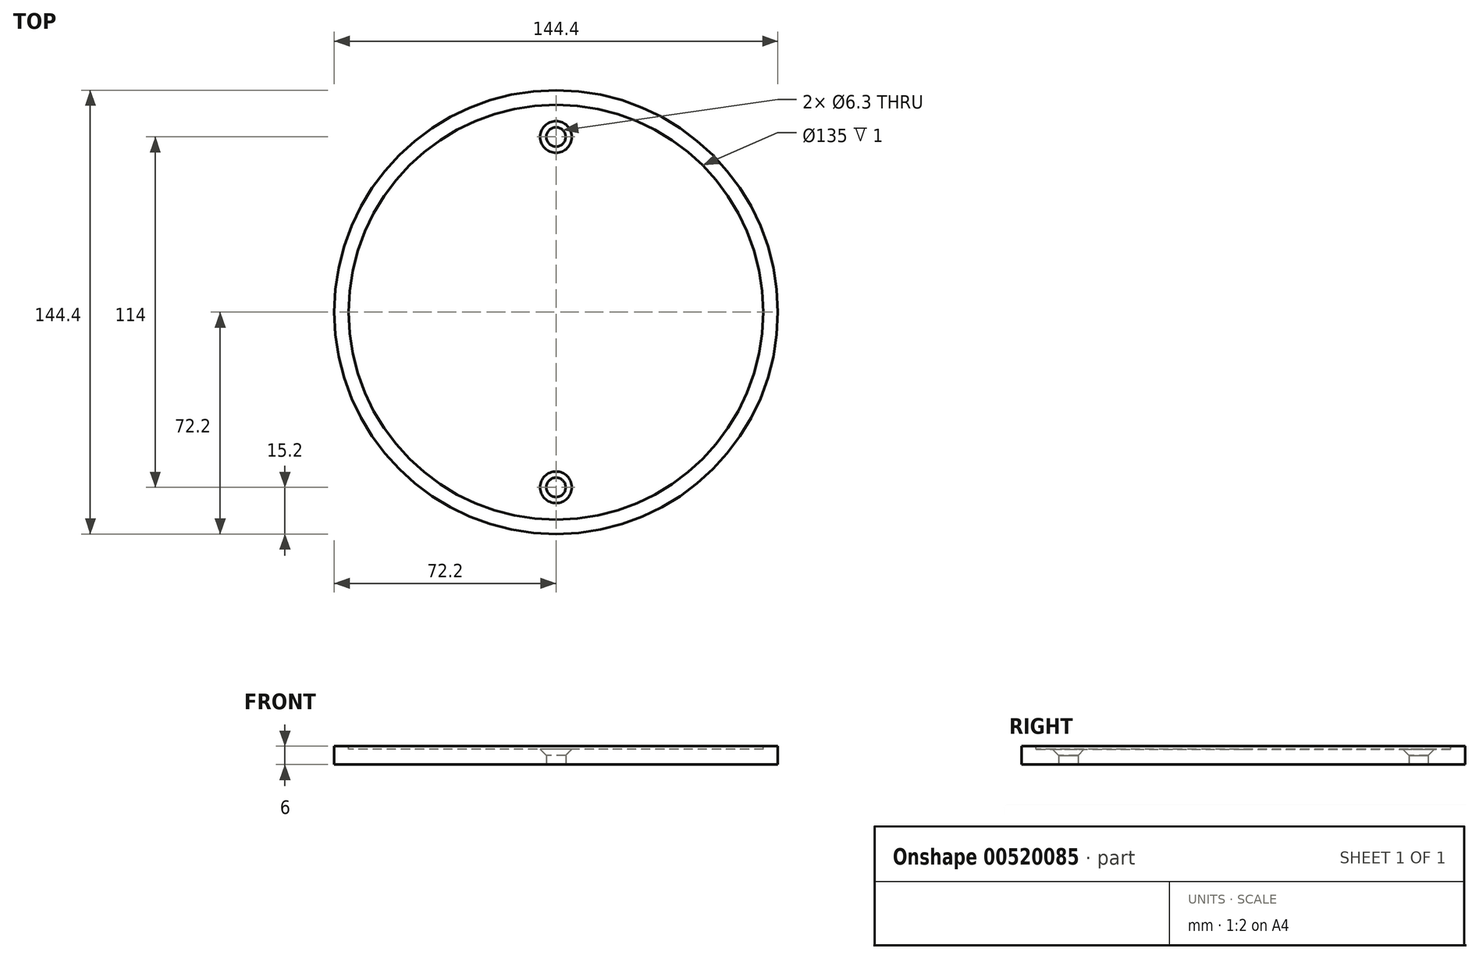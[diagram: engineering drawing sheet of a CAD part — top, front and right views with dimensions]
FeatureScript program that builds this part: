
annotation { "Feature Type Name" : "Feature", "Feature Type Description" : "" }
export const myFeature = defineFeature(function(context is Context, id is Id, definition is map)
    precondition{}
    {
        {
            var Q0;
            Q0=qCreatedBy(makeId("Top.planeOp"),FACE);
            var sketch = newSketch(context, id + "F0", { "sketchPlane" : qUnion([Q0])});
            skCircle(sketch, "E0", {"center": v(0, 0) * mm, "radius": 24.07 * mm});
            skCircle(sketch, "E1", {"center": v(0, 19) * mm, "radius": 1.05 * mm});
            skCircle(sketch, "E2", {"center": v(0, -19) * mm, "radius": 1.05 * mm});
            skSolve(sketch);
        }
        {
            var Q0;
            Q0=makeQuery(id+"F0.imprint","IMPRINT",FACE,{"disambiguationData":[TD([[makeQuery(id+"F0.imprint","IMPRINT",EDGE,{"derivedFrom":sQuery(id+"F0.wireOp",EDGE,"E0")}),1.0]])]});
            extrude(context, id + "F1", {"entities" : qUnion([Q0]), "depth" : 2 * mm});
        }
        {
            var Q0;
            Q0=makeQuery(id+"F1.opExtrude","CAP_EDGE",EDGE,{"disambiguationData":[OSD([sQuery(id+"F0.wireOp",EDGE,"E1")])],"isStart":false});
            var Q1;
            Q1=makeQuery(id+"F1.opExtrude","CAP_EDGE",EDGE,{"disambiguationData":[OSD([sQuery(id+"F0.wireOp",EDGE,"E2")])],"isStart":false});
            chamfer(context, id + "F2", {"entities" : qUnion([Q0, Q1]), "width" : 1 * mm, "tangentPropagation" : true});
        }
        {
            var Q0;
            Q0=makeQuery(id+"F1.opExtrude","SWEPT_BODY",BODY,{"disambiguationData":[OSD([sQuery(id+"F0.wireOp",EDGE,"E0"),sQuery(id+"F0.wireOp",EDGE,"E1"),sQuery(id+"F0.wireOp",EDGE,"E2")])]});
            var Q1;
            Q1=qCreatedBy(makeId("Origin.pointOp"),VERTEX);
            transform(context, id + "F3", {"entities" : qUnion([Q0]), "transformType" : TransformType.SCALE_UNIFORMLY, "scale" : 3, "makeCopy" : false, "scalePoint" : qUnion([Q1])});
        }
        {
            var Q0;
            Q0=makeQuery(id+"F1.opExtrude","CAP_FACE",FACE,{"disambiguationData":[OSD([sQuery(id+"F0.wireOp",EDGE,"E0"),sQuery(id+"F0.wireOp",EDGE,"E1"),sQuery(id+"F0.wireOp",EDGE,"E2")])],"isStart":false});
            var sketch = newSketch(context, id + "F4", { "sketchPlane" : qUnion([Q0])});
            skCircle(sketch, "E3", {"center": v(0, 0) * mm, "radius": 67.5 * mm});
            skSolve(sketch);
        }
        {
            var Q0;
            Q0=qSketchRegion(id+"F4",true);
            extrude(context, id + "F5", {"entities" : qUnion([Q0]), "operationType" : NewBodyOperationType.REMOVE, "oppositeDirection" : true, "depth" : 1 * mm});
        }
    });
